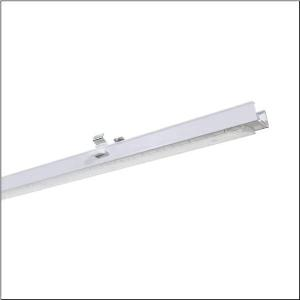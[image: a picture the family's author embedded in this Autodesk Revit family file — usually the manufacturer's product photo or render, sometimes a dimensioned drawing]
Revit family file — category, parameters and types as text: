
# Revit family: trunking_flex_31_51re14ma66b
name_source: partatom
category: Lighting Fixtures
units: mm (PartAtom-declared; Revit-internal decimal feet)

## family parameters
Cut with Voids When Loaded = No
Host = Face
Light Source = No
Part Type = Normal
Room Calculation Point = No
Round Connector Dimension = Use Diameter
Shared = No

## types (1)
- --- (1 x LED, 6400 lm, 40 W, 6500K)
    Apparent Load = 40 VA
    CIE Flux Codes = 72 92 98 99 100
    Color Rendering = 80
    Color Temperature = 6500K
    Default Elevation = 1800 mm
    Description = Trunking Flex 31, luminaire insert, of extruded aluminium section, coated, traffic white (RAL 9016), length: 1.172mm, width: 91mm, height: 53mm, LED rated luminous flux: 6.400lm, light colour: 865, control gear: ON/OFF Multilumen, with system connector: socket, mains connection: 220..240V, AC, 50/60Hz, rated input power: 40W, luminous flux adjustable on luminaire in four steps (3420/4540/5580/6630lm), connected load according to luminous flux setting (20/26/33/40W), primary light control with lens, of plastic, primary optical cover: cover, of PMMA, light emission: direct distribution, primary light characteristic: asymmetric, protection rating (complete): IP20, insulation class (complete): insulation class I (protective earthing), certification: CE, UKCA, impact resistance: IK02, permissible ambient temperature for indoor applications: -20..+40°C, packaging unit: 1 piece
    Height = 58 mm
    Lamp = 1 x LED
    Lamp Light Flux = 6400 lm
    Lamp Power = 40 W
    Lamp count = 1
    Length = 1172 mm
    Luminous efficacy = 160 lm/W
    Manufacturer = Siteco
    ModVariant = No
    Model = 51RE14MA66B
    Mounting Place = Ceiling
    Mounting Type = Pendant
    Number of Poles = 1
    OnlyDefault = Yes
    Power Factor = 1
    Product Name = Trunking Flex 31
    Product group = luminaire insert
    ProductGroupID = 901
    Protection Class = Protection class I
    Protection Degree = IP 20
    RLX_Detail_Level = 1
    RLX_Emergency_Light_Flux = 0 lm
    RLX_Emergency_Type = 0
    RLX_Emergency_Type_DB = No
    RlxData = <blob elided: 20653 chars, md5=86d8d13a>
    Socket = socket
    Standby Power = 0 W
    System Light Flux = 6400 lm
    System Power = 40 W
    Type Comments = factory setting: luminous flux: 100 % | (ON | ON) | 300 mA
    Type Image = l_1266702.jpg
    URL = http://relux.com
    VarID = @adj_001383
    Voltage = 0 V
    Weight = 0.00 kg
    Width = 65 mm

## geometry (parser evidence)
native form markers: Blend x4, Sweep x11
no freeform markers — native parametric forms only
